# Revit family: Control_Panels-Lutron-T-Series-Node
name_source: partatom
category: Electrical Equipment
revit_build: Autodesk Revit 2017 (Build: 20160225_1515(x64)
units: mm (PartAtom-declared; Revit-internal decimal feet)

## family parameters
Cut with Voids When Loaded = No
Host = Face
OmniClass Number = 23.80.30.11.17
OmniClass Title = Distribution Boards and Control Panels
Panel Configuration = Two Columns, Circuits Across
Part Type = Panelboard
Room Calculation Point = No
Round Connector Dimension = Use Radius
Shared = No

## types (1)
- QSN-TW
    Cost = 0 $
    Default Elevation = 0 "
    Description = T-Series Energi Savr Node Unit
    Electrical Potential = 120 V
    Feed Through Control Circuit Voltage = 120 V
    Finish = Steel - Lutron - Black
    Frequency = 60 Hz
    Ground Bus = No
    Instruction Sheet Link = http://www.lutron.com
    Load Classification = Power
    MCB Rating = 1 A
    Manufacturer = Lutron Electronics Co., Inc
    Manufacturer Fax Number = 610-282-1243
    Model = QSN-TW
    Neutral Bus = No
    Neutral Rating = 0.00%
    Number of Poles = 1
    Overall Depth = 3.16 "
    Overall Height = 13.25 "
    Overall Width = 9.25 "
    Performance URL = http://www.lutron.com
    Phase = 1
    Power Factor = 1
    Product Documentation Link = http://www.lutron.com
    Product Name = Energi Savr Node
    Product Page URL = http://www.lutron.com
    Series = Quantum
    SubFeed Lugs = No
    URL = http://www.lutron.com
    Unit Weight = 0.00 lb
    Version = 2017 - v1.0a
    Video Link = https://www.youtube.com
    Voltage = 120‑277 V~
    Warranty URL = http://www.lutron.com

## geometry (parser evidence)
native form markers: Sweep x2
no freeform markers — native parametric forms only
